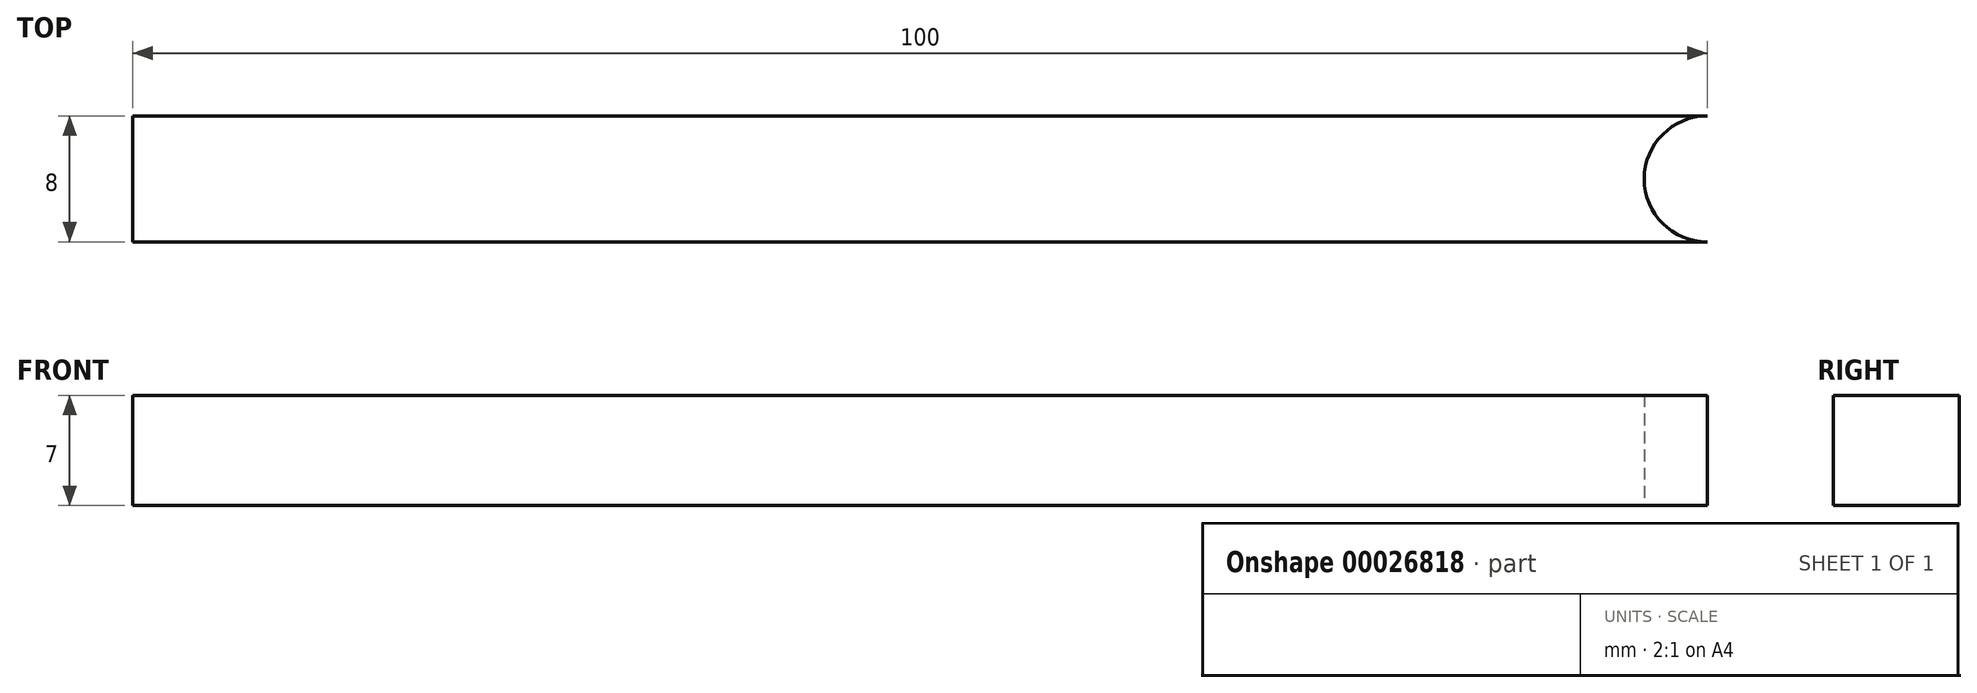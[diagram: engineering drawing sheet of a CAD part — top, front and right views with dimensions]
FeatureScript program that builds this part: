
annotation { "Feature Type Name" : "Feature", "Feature Type Description" : "" }
export const myFeature = defineFeature(function(context is Context, id is Id, definition is map)
    precondition{}
    {
        {
            var Q0;
            Q0=qCreatedBy(makeId("Top.planeOp"),FACE);
            var sketch = newSketch(context, id + "F0", { "sketchPlane" : qUnion([Q0])});
            skLineSegment(sketch, "E0.bottom", {"start": v(-49.97, 5.95) * mm, "end": v(50.03, 5.95) * mm});
            skLineSegment(sketch, "E0.top", {"start": v(-49.97, -2.05) * mm, "end": v(50.03, -2.05) * mm});
            skLineSegment(sketch, "E0.left", {"start": v(-49.97, 5.95) * mm, "end": v(-49.97, -2.05) * mm});
            skArc(sketch, "E1", {"start": v(50.03, 5.95) * mm, "mid": v(46.03, 1.95) * mm, "end": v(50.03, -2.05) * mm});
            skSolve(sketch);
        }
        {
            var Q0;
            Q0=makeQuery(id+"F0.imprint","IMPRINT",FACE,{"disambiguationData":[TD([[makeQuery(id+"F0.imprint","IMPRINT",EDGE,{"derivedFrom":sQuery(id+"F0.wireOp",EDGE,"E0.bottom")}),-1.0]])]});
            extrude(context, id + "F1", {"entities" : qUnion([Q0]), "depth" : 7 * mm});
        }
    });
